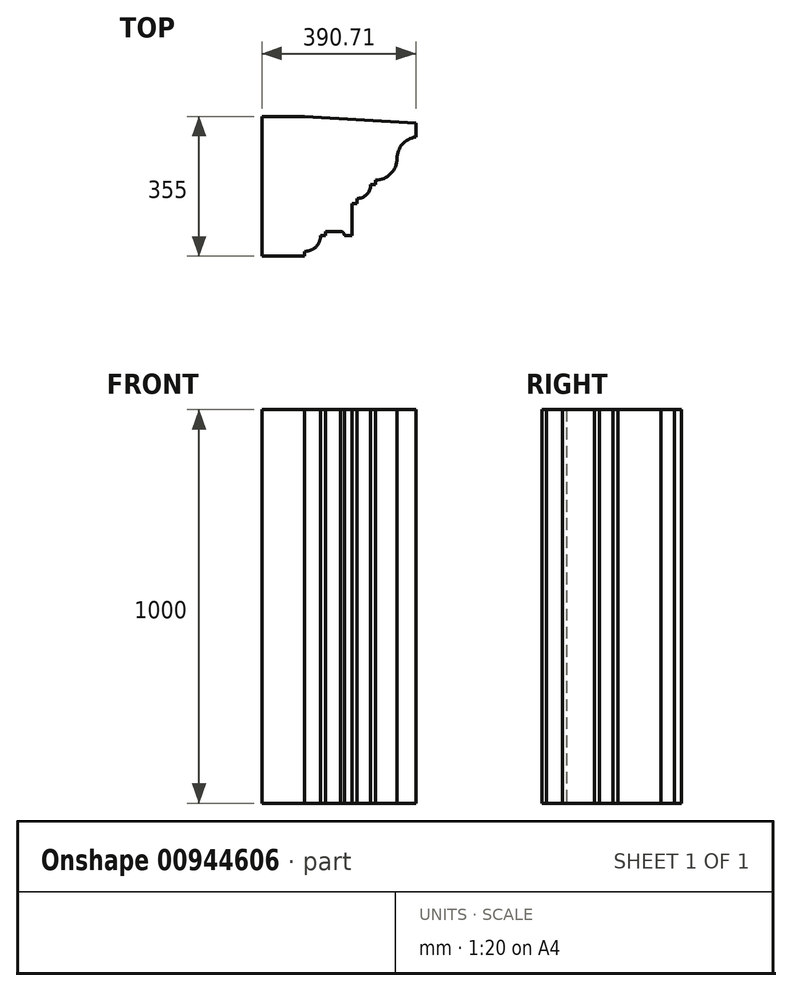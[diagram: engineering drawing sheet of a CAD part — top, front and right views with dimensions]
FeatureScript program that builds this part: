
annotation { "Feature Type Name" : "Feature", "Feature Type Description" : "" }
export const myFeature = defineFeature(function(context is Context, id is Id, definition is map)
    precondition{}
    {
        {
            var Q0;
            Q0=qCreatedBy(makeId("Top.planeOp"),FACE);
            var sketch = newSketch(context, id + "F0", { "sketchPlane" : qUnion([Q0])});
            skLineSegment(sketch, "E0", {"start": v(0, 0) * mm, "end": v(0, 355) * mm});
            skLineSegment(sketch, "E1", {"start": v(0, 355) * mm, "end": v(107.5, 355) * mm});
            skLineSegment(sketch, "E2", {"start": v(0, 0) * mm, "end": v(107.5, 0) * mm});
            skLineSegment(sketch, "E3", {"start": v(107.5, 0) * mm, "end": v(107.5, 12) * mm});
            skLineSegment(sketch, "E4", {"start": v(160.8, 62.77) * mm, "end": v(198.8, 62.77) * mm});
            skLineSegment(sketch, "E5", {"start": v(209.07, 52.77) * mm, "end": v(229.07, 52.77) * mm});
            skLineSegment(sketch, "E6", {"start": v(229.07, 52.77) * mm, "end": v(229.07, 133.85) * mm});
            skLineSegment(sketch, "E7", {"start": v(229.07, 133.85) * mm, "end": v(241.07, 133.85) * mm});
            skLineSegment(sketch, "E8", {"start": v(241.07, 133.85) * mm, "end": v(241.07, 146.05) * mm});
            skArc(sketch, "E9", {"start": v(107.5, 12) * mm, "mid": v(136.91, 23.51) * mm, "end": v(148.8, 52.77) * mm});
            skLineSegment(sketch, "E10", {"start": v(148.8, 52.77) * mm, "end": v(160.8, 52.77) * mm});
            skLineSegment(sketch, "E11", {"start": v(160.8, 52.77) * mm, "end": v(160.8, 62.77) * mm});
            skArc(sketch, "E12", {"start": v(209.07, 52.77) * mm, "mid": v(206.05, 59.93) * mm, "end": v(198.8, 62.77) * mm});
            skArc(sketch, "E13", {"start": v(241.07, 146.05) * mm, "mid": v(265.82, 156.3) * mm, "end": v(276.07, 181.05) * mm});
            skLineSegment(sketch, "E14", {"start": v(276.07, 181.05) * mm, "end": v(288.07, 181.05) * mm});
            skLineSegment(sketch, "E15", {"start": v(288.07, 181.05) * mm, "end": v(288.07, 193.05) * mm});
            skArc(sketch, "E16", {"start": v(288.07, 193.05) * mm, "mid": v(326.96, 209.16) * mm, "end": v(343.07, 248.05) * mm});
            skArc(sketch, "E17", {"start": v(343.07, 248.05) * mm, "mid": v(356.66, 284.25) * mm, "end": v(390.71, 302.56) * mm});
            skLineSegment(sketch, "E18", {"start": v(390.71, 302.56) * mm, "end": v(390.71, 337.56) * mm});
            skLineSegment(sketch, "E19", {"start": v(390.71, 337.56) * mm, "end": v(107.5, 355) * mm});
            skSolve(sketch);
        }
        {
            var Q0;
            Q0=makeQuery(id+"F0.imprint","IMPRINT",FACE,{"disambiguationData":[TD([[makeQuery(id+"F0.imprint","IMPRINT",EDGE,{"derivedFrom":sQuery(id+"F0.wireOp",EDGE,"E0")}),-1.0]])]});
            extrude(context, id + "F1", {"entities" : qUnion([Q0]), "depth" : 1000 * mm, "offsetDistance" : 25 * mm});
        }
    });
